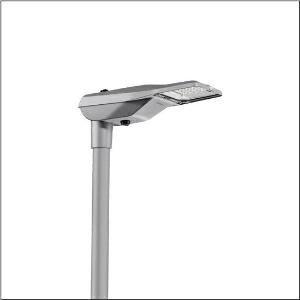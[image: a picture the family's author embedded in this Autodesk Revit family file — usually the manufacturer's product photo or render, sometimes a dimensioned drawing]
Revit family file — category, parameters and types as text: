
# Revit family: streetlight_sl_21_micro___st1_0a_5xe1d43t08db_894b
name_source: partatom
category: Lighting Fixtures
units: mm (PartAtom-declared; Revit-internal decimal feet)

## family parameters
Cut with Voids When Loaded = No
Host = Face
Light Source = No
Part Type = Normal
Room Calculation Point = No
Round Connector Dimension = Use Diameter
Shared = No

## types (1)
- --- (1 x LED, 5320 lm, 39.1 W, 4000K)
    Apparent Load = 39 VA
    CIE Flux Codes = 37 72 97 100 100
    Color Rendering = 70
    Color Temperature = 4000K
    Default Elevation = 1800 mm
    Description = Streetlight SL 21 micro, mast luminaire, primary light control with lens, of PMMA, primary optical cover: cover, of toughened safety glass, transparent, light distribution: ST1.0a, light emission: direct distribution, primary light characteristic: asymmetric, installation type: side-entry, post-top, LED, High Power LED, rated luminous flux: 5.320lm, luminous efficacy: 136lm/W, light colour: 740, colour temperature: 4000K, control: flexible luminous flux parameterisation, time-dependent luminous flux control, constant luminous flux control, overheat protection, presetting dimming logarithmic, mains connection: 220..240V, AC, 50/60Hz, start of lifetime: 39W, end of service life: 41W, reduction: 18W, luminaire housing, of diecast aluminium, powder-coated, Siteco® metallic grey (DB 702S), corrosivity category C5 mid according to DIN EN ISO 12944, please order mast flange separately, inclination adjustable: 0°, 5°, 10°, 15°, sealing non-destructively replaceable, multi-level sealing system, length: 528mm, width: 235mm, height: 110mm, mast flange for spigot size: 42mm (side-entry): 5XC10008XM4, 60/48mm (side-entry/post-top): 5XC10108XM2, 76/60mm (side-entry/post-top): 5XC10108XM1, Smart Interface below and above, protection rating (complete): IP66, insulation class (complete): insulation class II (safety insulation), certification: CE, ENEC, ENEC+, VDE, impact resistance: IK09, permissible operating ambient temperature for outdoor applications: -40..+50°C, standard-compliant lighting for roads and squares, packaging unit: 1 piece

Light Distribution: ST1.0a
    Height = 110 mm
    Lamp = 1 x LED
    Lamp Light Flux = 5320 lm
    Lamp Power = 39.1 W
    Lamp count = 1
    Length = 528 mm
    Luminous efficacy = 136 lm/W
    Manufacturer = Siteco
    ModVariant = No
    Model = 5XE1D43T08DB
    Number of Poles = 1
    OnlyDefault = Yes
    Power Factor = 1
    Product Name = Streetlight SL 21 micro | ST1.0a
    Product group = mast luminaire | pylon top
    ProductGroupID = 6100
    Protection Class = Protection class II
    Protection Degree = IP 66
    RLX_Detail_Level = 1
    RLX_Emergency_Light_Flux = 0 lm
    RLX_Emergency_Type = 0
    RLX_Emergency_Type_DB = No
    RlxData = <blob elided: 98669 chars, md5=78cba2be>
    Socket = socket
    Standby Power = 0 W
    System Light Flux = 5320 lm
    System Power = 39 W
    Type Comments = factory setting: luminous flux: 100 % | dim-lin: 254 | 765 mA
    Type Image = l_1007239.jpg
    URL = http://relux.com
    VarID = @adj_105877
    Voltage = 0 V
    Weight = 0.00 kg
    Width = 235 mm

## geometry (parser evidence)
native form markers: Blend x4, Sweep x9
no freeform markers — native parametric forms only
